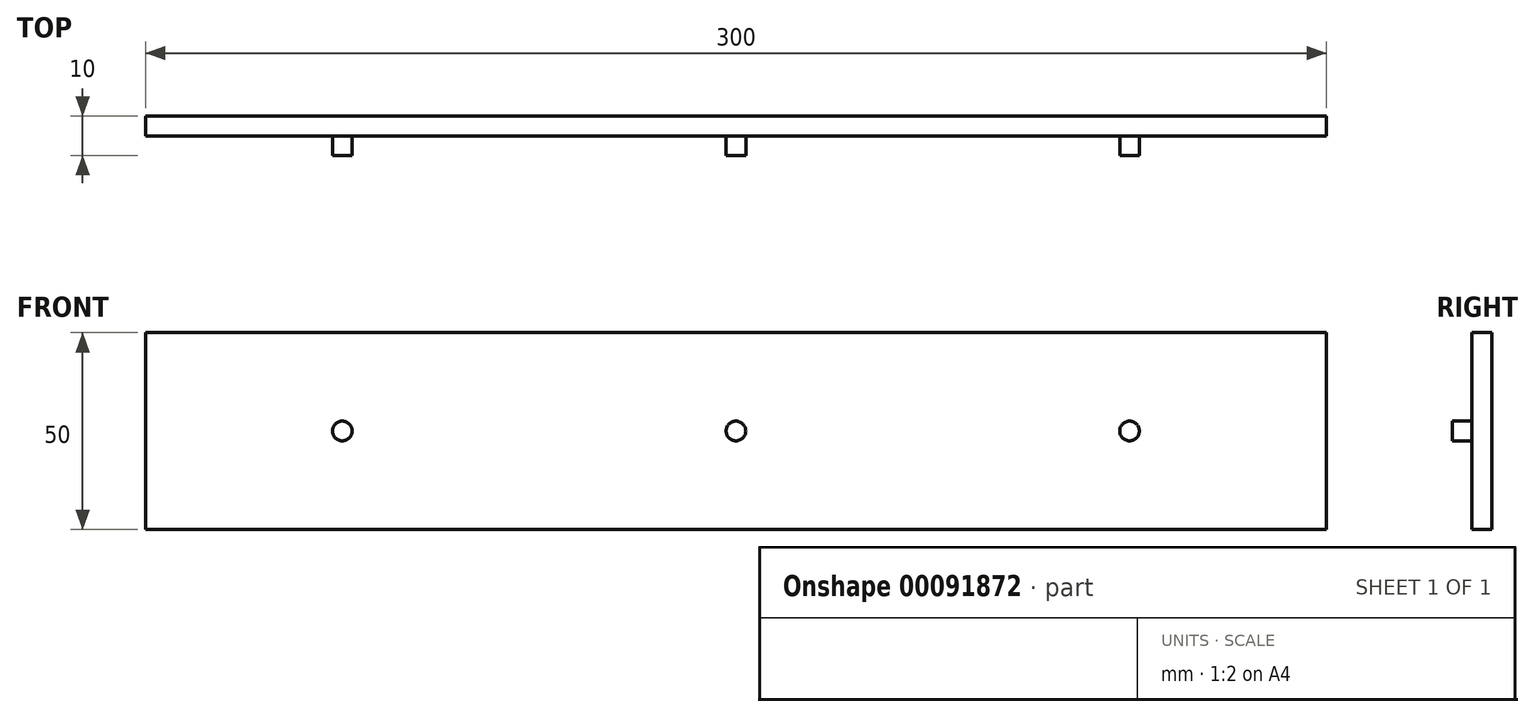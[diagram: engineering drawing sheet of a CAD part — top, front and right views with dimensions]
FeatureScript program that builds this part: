
annotation { "Feature Type Name" : "Feature", "Feature Type Description" : "" }
export const myFeature = defineFeature(function(context is Context, id is Id, definition is map)
    precondition{}
    {
        {
            var Q0;
            Q0=qCreatedBy(makeId("Front.planeOp"),FACE);
            var sketch = newSketch(context, id + "F0", { "sketchPlane" : qUnion([Q0])});
            skLineSegment(sketch, "E0.bottom", {"start": v(150, -25) * mm, "end": v(-150, -25) * mm});
            skLineSegment(sketch, "E0.top", {"start": v(150, 25) * mm, "end": v(-150, 25) * mm});
            skLineSegment(sketch, "E0.left", {"start": v(150, -25) * mm, "end": v(150, 25) * mm});
            skLineSegment(sketch, "E0.right", {"start": v(-150, -25) * mm, "end": v(-150, 25) * mm});
            skLineSegment(sketch, "E1", {"start": v(-150, 38.36) * mm, "end": v(-100, 38.36) * mm});
            skLineSegment(sketch, "E2", {"start": v(150, 33.39) * mm, "end": v(100, 33.39) * mm});
            skCircle(sketch, "E3", {"center": v(-100, 0) * mm, "radius": 2.5 * mm});
            skCircle(sketch, "E4", {"center": v(0, 0) * mm, "radius": 2.5 * mm});
            skCircle(sketch, "E5", {"center": v(100, 0) * mm, "radius": 2.5 * mm});
            skSolve(sketch);
        }
        {
            var Q0;
            Q0 = qSketchRegion(id + "F0", true);
            extrude(context, id + "F1", {"entities" : qUnion([Q0]), "depth" : 5 * mm});
        }
        {
            var Q0;
            Q0=makeQuery(id+"F0.imprint","IMPRINT",FACE,{"disambiguationData":[TD([[makeQuery(id+"F0.imprint","IMPRINT",EDGE,{"derivedFrom":sQuery(id+"F0.wireOp",EDGE,"E3")}),1.0]])]});
            var Q1;
            Q1=makeQuery(id+"F0.imprint","IMPRINT",FACE,{"disambiguationData":[TD([[makeQuery(id+"F0.imprint","IMPRINT",EDGE,{"derivedFrom":sQuery(id+"F0.wireOp",EDGE,"E4")}),1.0]])]});
            var Q2;
            Q2=makeQuery(id+"F0.imprint","IMPRINT",FACE,{"disambiguationData":[TD([[makeQuery(id+"F0.imprint","IMPRINT",EDGE,{"derivedFrom":sQuery(id+"F0.wireOp",EDGE,"E5")}),1.0]])]});
            extrude(context, id + "F2", {"entities" : qUnion([Q0, Q1, Q2]), "operationType" : NewBodyOperationType.ADD, "depth" : 10 * mm});
        }
    });
